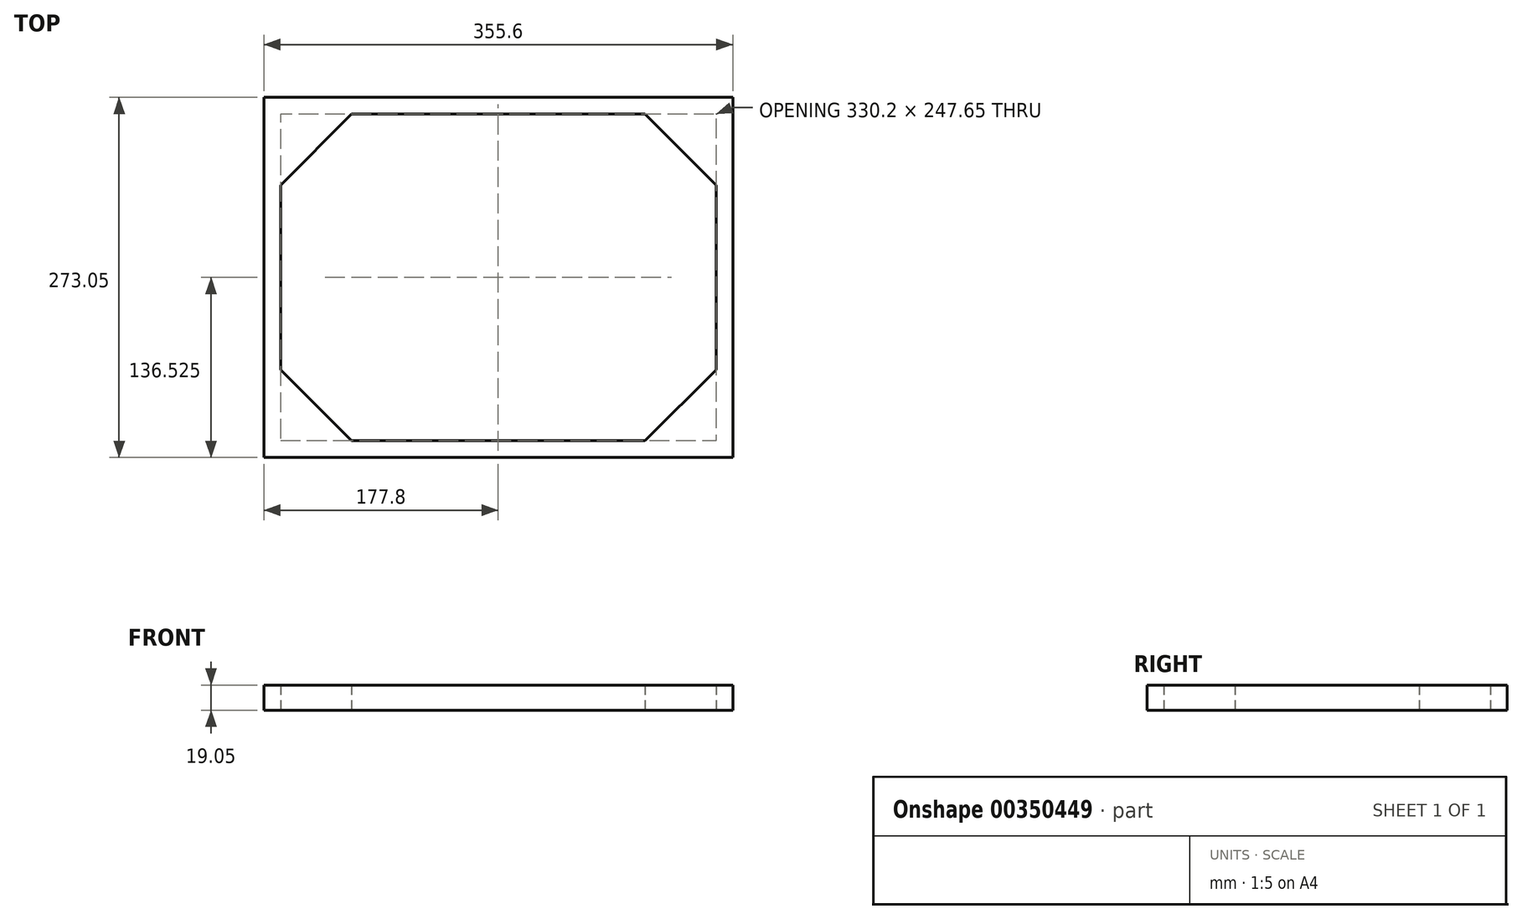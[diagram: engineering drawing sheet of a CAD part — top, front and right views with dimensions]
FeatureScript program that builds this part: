
annotation { "Feature Type Name" : "Feature", "Feature Type Description" : "" }
export const myFeature = defineFeature(function(context is Context, id is Id, definition is map)
    precondition{}
    {
        {
            var Q0;
            Q0=qCreatedBy(makeId("Top.planeOp"),FACE);
            var sketch = newSketch(context, id + "F0", { "sketchPlane" : qUnion([Q0])});
            skLineSegment(sketch, "E0", {"start": v(66.58, 260.35) * mm, "end": v(12.7, 206.47) * mm});
            skLineSegment(sketch, "E1", {"start": v(289.02, 260.35) * mm, "end": v(342.9, 206.47) * mm});
            skLineSegment(sketch, "E2", {"start": v(342.9, 66.58) * mm, "end": v(289.02, 12.7) * mm});
            skLineSegment(sketch, "E3", {"start": v(12.7, 66.58) * mm, "end": v(66.58, 12.7) * mm});
            skLineSegment(sketch, "E4", {"start": v(12.7, 206.47) * mm, "end": v(12.7, 66.58) * mm});
            skLineSegment(sketch, "E5", {"start": v(66.58, 12.7) * mm, "end": v(289.02, 12.7) * mm});
            skLineSegment(sketch, "E6", {"start": v(342.9, 66.58) * mm, "end": v(342.9, 206.47) * mm});
            skLineSegment(sketch, "E7", {"start": v(66.58, 260.35) * mm, "end": v(289.02, 260.35) * mm});
            skLineSegment(sketch, "E8.bottom", {"start": v(0, 273.05) * mm, "end": v(355.6, 273.05) * mm});
            skLineSegment(sketch, "E8.top", {"start": v(0, 0) * mm, "end": v(355.6, 0) * mm});
            skLineSegment(sketch, "E8.left", {"start": v(0, 273.05) * mm, "end": v(0, 0) * mm});
            skLineSegment(sketch, "E8.right", {"start": v(355.6, 273.05) * mm, "end": v(355.6, 0) * mm});
            skPoint(sketch, "E9", {"position": v(177.8, 273.05) * mm});
            skPoint(sketch, "E10", {"position": v(177.8, 260.35) * mm});
            skPoint(sketch, "E11", {"position": v(0, 136.52) * mm});
            skPoint(sketch, "E12", {"position": v(12.7, 136.52) * mm});
            skLineSegment(sketch, "E13", {"start": v(177.8, 260.35) * mm, "end": v(177.8, 273.05) * mm, "construction": true});
            skLineSegment(sketch, "E14", {"start": v(177.8, 0) * mm, "end": v(177.8, 12.7) * mm, "construction": true});
            skLineSegment(sketch, "E15", {"start": v(0, 136.52) * mm, "end": v(12.7, 136.52) * mm, "construction": true});
            skLineSegment(sketch, "E16", {"start": v(342.9, 136.53) * mm, "end": v(355.6, 136.52) * mm, "construction": true});
            skSolve(sketch);
        }
        {
            var Q0;
            Q0=makeQuery(id+"F0.imprint","IMPRINT",FACE,{"disambiguationData":[TD([[makeQuery(id+"F0.imprint","IMPRINT",EDGE,{"derivedFrom":sQuery(id+"F0.wireOp",EDGE,"E0")}),-1.0]])]});
            extrude(context, id + "F1", {"entities" : qUnion([Q0]), "depth" : 19.05 * mm});
        }
    });
